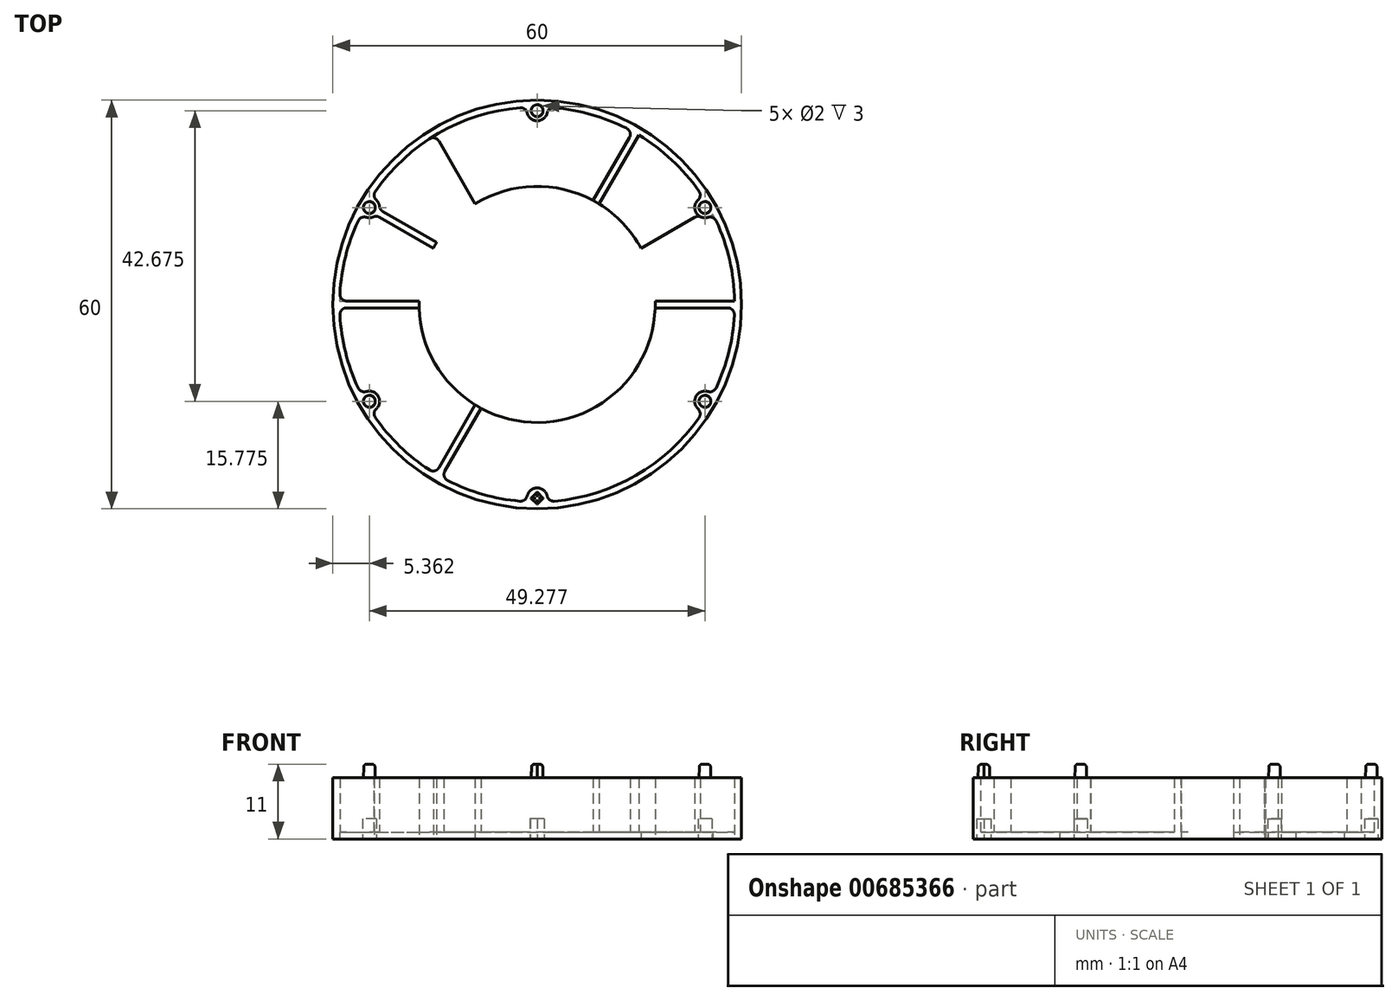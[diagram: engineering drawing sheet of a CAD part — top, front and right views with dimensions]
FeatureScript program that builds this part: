
annotation { "Feature Type Name" : "Feature", "Feature Type Description" : "" }
export const myFeature = defineFeature(function(context is Context, id is Id, definition is map)
    precondition{}
    {
        {
            var Q0;
            Q0=qCreatedBy(makeId("Top.planeOp"),FACE);
            var sketch = newSketch(context, id + "F0", { "sketchPlane" : qUnion([Q0])});
            skCircle(sketch, "E0", {"center": v(0, 0) * mm, "radius": 30 * mm});
            skCircle(sketch, "E1.0", {"center": v(0, 0) * mm, "radius": 29 * mm});
            skLineSegment(sketch, "E2.bottom", {"start": v(14.56, 26.23) * mm, "end": v(15.43, 25.73) * mm});
            skLineSegment(sketch, "E2.top", {"start": v(-15.43, -25.73) * mm, "end": v(-14.56, -26.23) * mm});
            skLineSegment(sketch, "E2.left", {"start": v(14.56, 26.23) * mm, "end": v(-15.43, -25.73) * mm});
            skLineSegment(sketch, "E2.right", {"start": v(15.43, 25.73) * mm, "end": v(-14.56, -26.23) * mm});
            skLineSegment(sketch, "E3.bottom", {"start": v(25.73, 15.43) * mm, "end": v(26.23, 14.56) * mm});
            skLineSegment(sketch, "E3.top", {"start": v(-26.23, -14.56) * mm, "end": v(-25.73, -15.43) * mm});
            skLineSegment(sketch, "E3.left", {"start": v(25.73, 15.43) * mm, "end": v(-26.23, -14.56) * mm});
            skLineSegment(sketch, "E3.right", {"start": v(26.23, 14.56) * mm, "end": v(-25.73, -15.43) * mm});
            skLineSegment(sketch, "E4", {"start": v(-38.35, 0) * mm, "end": v(39.17, 0) * mm, "construction": true});
            skLineSegment(sketch, "E5", {"start": v(0, 42.5) * mm, "end": v(0, -42.47) * mm, "construction": true});
            skLineSegment(sketch, "E6.bottom", {"start": v(-30, 0.5) * mm, "end": v(30, 0.5) * mm});
            skLineSegment(sketch, "E6.top", {"start": v(-30, -0.5) * mm, "end": v(30, -0.5) * mm});
            skLineSegment(sketch, "E6.left", {"start": v(-30, 0.5) * mm, "end": v(-30, -0.5) * mm});
            skLineSegment(sketch, "E6.right", {"start": v(30, 0.5) * mm, "end": v(30, -0.5) * mm});
            skLineSegment(sketch, "E7.bottom", {"start": v(-25.73, 15.43) * mm, "end": v(26.23, -14.56) * mm});
            skLineSegment(sketch, "E7.top", {"start": v(-26.23, 14.56) * mm, "end": v(25.73, -15.43) * mm});
            skLineSegment(sketch, "E7.left", {"start": v(-25.73, 15.43) * mm, "end": v(-26.23, 14.56) * mm});
            skLineSegment(sketch, "E7.right", {"start": v(26.23, -14.56) * mm, "end": v(25.73, -15.43) * mm});
            skLineSegment(sketch, "E8.bottom", {"start": v(-0.5, 30) * mm, "end": v(0.5, 30) * mm});
            skLineSegment(sketch, "E8.top", {"start": v(-0.5, -30) * mm, "end": v(0.5, -30) * mm});
            skLineSegment(sketch, "E8.left", {"start": v(-0.5, 30) * mm, "end": v(-0.5, -30) * mm});
            skLineSegment(sketch, "E8.right", {"start": v(0.5, 30) * mm, "end": v(0.5, -30) * mm});
            skLineSegment(sketch, "E9.bottom", {"start": v(-15.43, 25.73) * mm, "end": v(-14.56, 26.23) * mm});
            skLineSegment(sketch, "E9.top", {"start": v(14.56, -26.23) * mm, "end": v(15.43, -25.73) * mm});
            skLineSegment(sketch, "E9.left", {"start": v(-15.43, 25.73) * mm, "end": v(14.56, -26.23) * mm});
            skLineSegment(sketch, "E9.right", {"start": v(-14.56, 26.23) * mm, "end": v(15.43, -25.73) * mm});
            skCircle(sketch, "E10", {"center": v(0, 0) * mm, "radius": 17.33 * mm});
            skSolve(sketch);
        }
        {
            var Q0;
            Q0=qCreatedBy(makeId("Top.planeOp"),FACE);
            var sketch = newSketch(context, id + "F1", { "sketchPlane" : qUnion([Q0])});
            skCircle(sketch, "E11", {"center": v(0, 0) * mm, "radius": 30 * mm});
            skCircle(sketch, "E12", {"center": v(0, 0) * mm, "radius": 29 * mm});
            skSolve(sketch);
        }
        {
            var Q0;
            Q0=makeQuery(id+"F1.imprint","IMPRINT",FACE,{"disambiguationData":[TD([[makeQuery(id+"F1.imprint","IMPRINT",EDGE,{"derivedFrom":sQuery(id+"F1.wireOp",EDGE,"E11")}),1.0]])]});
            extrude(context, id + "F2", {"entities" : qUnion([Q0]), "depth" : 9 * mm, "offsetDistance" : 25 * mm});
        }
        {
            var Q0;
            {var subQ0=sQuery(id+"F0.wireOp",EDGE,"E7.bottom");var subQ1=sQuery(id+"F0.wireOp",EDGE,"E1.0");var subQ2=makeQuery(id+"F0.imprint","INTERSECT",VERTEX,{"disambiguationData":[OD(0.0)],"derivedFrom":[subQ1,subQ0]});Q0=makeQuery(id+"F0.imprint","IMPRINT",FACE,{"disambiguationData":[TD([[makeQuery(id+"F0.imprint","IMPRINT",EDGE,{"disambiguationData":[TD([[subQ2,-1.0]])],"derivedFrom":subQ1}),1.0]])]});}
            var Q1;
            {var subQ0=sQuery(id+"F0.wireOp",EDGE,"E2.right");var subQ1=sQuery(id+"F0.wireOp",EDGE,"E1.0");var subQ2=makeQuery(id+"F0.imprint","INTERSECT",VERTEX,{"disambiguationData":[OD(0.0)],"derivedFrom":[subQ1,subQ0]});Q1=makeQuery(id+"F0.imprint","IMPRINT",FACE,{"disambiguationData":[TD([[makeQuery(id+"F0.imprint","IMPRINT",EDGE,{"disambiguationData":[TD([[subQ2,-1.0]])],"derivedFrom":subQ1}),1.0]])]});}
            var Q2;
            {var subQ0=sQuery(id+"F0.wireOp",EDGE,"E6.bottom");var subQ1=sQuery(id+"F0.wireOp",EDGE,"E1.0");var subQ2=makeQuery(id+"F0.imprint","INTERSECT",VERTEX,{"disambiguationData":[OD(0.0)],"derivedFrom":[subQ1,subQ0]});Q2=makeQuery(id+"F0.imprint","IMPRINT",FACE,{"disambiguationData":[TD([[makeQuery(id+"F0.imprint","IMPRINT",EDGE,{"disambiguationData":[TD([[subQ2,1.0]])],"derivedFrom":subQ1}),1.0]])]});}
            var Q3;
            {var subQ0=sQuery(id+"F0.wireOp",EDGE,"E2.left");var subQ1=sQuery(id+"F0.wireOp",EDGE,"E1.0");var subQ2=makeQuery(id+"F0.imprint","INTERSECT",VERTEX,{"disambiguationData":[OD(1.0)],"derivedFrom":[subQ1,subQ0]});Q3=makeQuery(id+"F0.imprint","IMPRINT",FACE,{"disambiguationData":[TD([[makeQuery(id+"F0.imprint","IMPRINT",EDGE,{"disambiguationData":[TD([[subQ2,-1.0]])],"derivedFrom":subQ1}),1.0]])]});}
            var Q4;
            {var subQ0=sQuery(id+"F0.wireOp",EDGE,"E6.bottom");var subQ1=sQuery(id+"F0.wireOp",EDGE,"E1.0");var subQ2=makeQuery(id+"F0.imprint","INTERSECT",VERTEX,{"disambiguationData":[OD(1.0)],"derivedFrom":[subQ1,subQ0]});Q4=makeQuery(id+"F0.imprint","IMPRINT",FACE,{"disambiguationData":[TD([[makeQuery(id+"F0.imprint","IMPRINT",EDGE,{"disambiguationData":[TD([[subQ2,-1.0]])],"derivedFrom":subQ1}),1.0]])]});}
            extrude(context, id + "F3", {"entities" : qUnion([Q0, Q1, Q2, Q3, Q4]), "operationType" : NewBodyOperationType.ADD, "depth" : 9 * mm, "offsetDistance" : 25 * mm});
        }
        {
            var Q0;
            Q0=makeQuery(id+"F1.imprint","IMPRINT",FACE,{"disambiguationData":[TD([[makeQuery(id+"F1.imprint","IMPRINT",EDGE,{"derivedFrom":sQuery(id+"F1.wireOp",EDGE,"E11")}),1.0]])]});
            var Q1;
            Q1=makeQuery(id+"F1.imprint","IMPRINT",FACE,{"disambiguationData":[TD([[makeQuery(id+"F1.imprint","IMPRINT",EDGE,{"derivedFrom":sQuery(id+"F1.wireOp",EDGE,"E12")}),1.0]])]});
            extrude(context, id + "F4", {"entities" : qUnion([Q0, Q1]), "operationType" : NewBodyOperationType.ADD, "depth" : 1 * mm, "offsetDistance" : 25 * mm});
        }
        {
            var Q0;
            {var subQ0=sQuery(id+"F0.wireOp",EDGE,"E3.right");var subQ1=sQuery(id+"F0.wireOp",EDGE,"E1.0");var subQ2=makeQuery(id+"F0.imprint","INTERSECT",VERTEX,{"disambiguationData":[OD(0.0)],"derivedFrom":[subQ1,subQ0]});Q0=makeQuery(id+"F0.imprint","IMPRINT",FACE,{"disambiguationData":[TD([[makeQuery(id+"F0.imprint","IMPRINT",EDGE,{"disambiguationData":[TD([[subQ2,1.0]])],"derivedFrom":subQ1}),1.0]])]});}
            var Q1;
            {var subQ0=sQuery(id+"F0.wireOp",EDGE,"E9.left");var subQ1=sQuery(id+"F0.wireOp",EDGE,"E1.0");var subQ2=makeQuery(id+"F0.imprint","INTERSECT",VERTEX,{"disambiguationData":[OD(0.0)],"derivedFrom":[subQ1,subQ0]});Q1=makeQuery(id+"F0.imprint","IMPRINT",FACE,{"disambiguationData":[TD([[makeQuery(id+"F0.imprint","IMPRINT",EDGE,{"disambiguationData":[TD([[subQ2,-1.0]])],"derivedFrom":subQ1}),1.0]])]});}
            var Q2;
            {var subQ0=sQuery(id+"F0.wireOp",EDGE,"E7.top");var subQ1=sQuery(id+"F0.wireOp",EDGE,"E1.0");var subQ2=makeQuery(id+"F0.imprint","INTERSECT",VERTEX,{"disambiguationData":[OD(0.0)],"derivedFrom":[subQ1,subQ0]});Q2=makeQuery(id+"F0.imprint","IMPRINT",FACE,{"disambiguationData":[TD([[makeQuery(id+"F0.imprint","IMPRINT",EDGE,{"disambiguationData":[TD([[subQ2,-1.0]])],"derivedFrom":subQ1}),1.0]])]});}
            extrude(context, id + "F5", {"entities" : qUnion([Q0, Q1, Q2]), "operationType" : NewBodyOperationType.REMOVE, "depth" : 1 * mm, "offsetDistance" : 25 * mm});
        }
        {
            var Q0;
            Q0=qCreatedBy(makeId("Top.planeOp"),FACE);
            var sketch = newSketch(context, id + "F6", { "sketchPlane" : qUnion([Q0])});
            skCircle(sketch, "E13", {"center": v(0, 0) * mm, "radius": 28.45 * mm});
            skLineSegment(sketch, "E14", {"start": v(0, 28.45) * mm, "end": v(0, -28.45) * mm, "construction": true});
            skLineSegment(sketch, "E15", {"start": v(24.64, 14.22) * mm, "end": v(0, 0) * mm, "construction": true});
            skLineSegment(sketch, "E16", {"start": v(14.23, 24.64) * mm, "end": v(0, 0) * mm, "construction": true});
            skLineSegment(sketch, "E17", {"start": v(0, 0) * mm, "end": v(28.45, 0) * mm, "construction": true});
            skLineSegment(sketch, "E18", {"start": v(0, 0) * mm, "end": v(24.64, -14.22) * mm, "construction": true});
            skLineSegment(sketch, "E19", {"start": v(0, 0) * mm, "end": v(14.23, -24.64) * mm, "construction": true});
            skLineSegment(sketch, "E20", {"start": v(0, 0) * mm, "end": v(-14.23, 24.64) * mm, "construction": true});
            skLineSegment(sketch, "E21", {"start": v(0, 0) * mm, "end": v(-24.64, 14.22) * mm, "construction": true});
            skLineSegment(sketch, "E22", {"start": v(0, 0) * mm, "end": v(-28.45, 0) * mm, "construction": true});
            skLineSegment(sketch, "E23", {"start": v(0, 0) * mm, "end": v(-24.64, -14.23) * mm, "construction": true});
            skLineSegment(sketch, "E24", {"start": v(0, 0) * mm, "end": v(-14.22, -24.64) * mm, "construction": true});
            skCircle(sketch, "E25", {"center": v(0, 28.45) * mm, "radius": 1.5 * mm});
            skCircle(sketch, "E26", {"center": v(24.64, 14.22) * mm, "radius": 1.5 * mm});
            skCircle(sketch, "E27", {"center": v(24.64, -14.22) * mm, "radius": 1.5 * mm});
            skCircle(sketch, "E28", {"center": v(0, -28.45) * mm, "radius": 1.5 * mm});
            skCircle(sketch, "E29", {"center": v(-24.64, -14.23) * mm, "radius": 1.5 * mm});
            skCircle(sketch, "E30", {"center": v(-24.64, 14.22) * mm, "radius": 1.5 * mm});
            skCircle(sketch, "E31", {"center": v(-24.64, 14.22) * mm, "radius": 1 * mm});
            skCircle(sketch, "E32", {"center": v(0, 28.45) * mm, "radius": 1 * mm});
            skCircle(sketch, "E33", {"center": v(24.64, 14.22) * mm, "radius": 1 * mm});
            skCircle(sketch, "E34", {"center": v(24.64, -14.22) * mm, "radius": 1 * mm});
            skCircle(sketch, "E35", {"center": v(-24.64, -14.23) * mm, "radius": 1 * mm});
            skLineSegment(sketch, "E36.bottom", {"start": v(1.06, -28.45) * mm, "end": v(0, -29.51) * mm});
            skLineSegment(sketch, "E36.top", {"start": v(0, -27.39) * mm, "end": v(-1.06, -28.45) * mm});
            skLineSegment(sketch, "E36.left", {"start": v(1.06, -28.45) * mm, "end": v(0, -27.39) * mm});
            skLineSegment(sketch, "E36.right", {"start": v(0, -29.51) * mm, "end": v(-1.06, -28.45) * mm});
            skSolve(sketch);
        }
        {
            var Q0;
            {var subQ0=sQuery(id+"F6.wireOp",EDGE,"E30");var subQ1=sQuery(id+"F6.wireOp",EDGE,"E13");var subQ2=makeQuery(id+"F6.imprint","INTERSECT",VERTEX,{"disambiguationData":[OD(0.0)],"derivedFrom":[subQ1,subQ0]});Q0=makeQuery(id+"F6.imprint","IMPRINT",FACE,{"disambiguationData":[TD([[makeQuery(id+"F6.imprint","IMPRINT",EDGE,{"disambiguationData":[TD([[subQ2,-1.0]])],"derivedFrom":subQ1}),1.0]])]});}
            var Q1;
            {var subQ0=sQuery(id+"F6.wireOp",EDGE,"E30");var subQ1=sQuery(id+"F6.wireOp",EDGE,"E13");var subQ2=makeQuery(id+"F6.imprint","INTERSECT",VERTEX,{"disambiguationData":[OD(0.0)],"derivedFrom":[subQ1,subQ0]});Q1=makeQuery(id+"F6.imprint","IMPRINT",FACE,{"disambiguationData":[TD([[makeQuery(id+"F6.imprint","IMPRINT",EDGE,{"disambiguationData":[TD([[subQ2,-1.0]])],"derivedFrom":subQ1}),-1.0]])]});}
            var Q2;
            {var subQ0=sQuery(id+"F6.wireOp",EDGE,"E25");var subQ1=sQuery(id+"F6.wireOp",EDGE,"E13");var subQ2=makeQuery(id+"F6.imprint","INTERSECT",VERTEX,{"disambiguationData":[OD(0.0)],"derivedFrom":[subQ1,subQ0]});Q2=makeQuery(id+"F6.imprint","IMPRINT",FACE,{"disambiguationData":[TD([[makeQuery(id+"F6.imprint","IMPRINT",EDGE,{"disambiguationData":[TD([[subQ2,-1.0]])],"derivedFrom":subQ1}),1.0]])]});}
            var Q3;
            {var subQ0=sQuery(id+"F6.wireOp",EDGE,"E25");var subQ1=sQuery(id+"F6.wireOp",EDGE,"E13");var subQ2=makeQuery(id+"F6.imprint","INTERSECT",VERTEX,{"disambiguationData":[OD(0.0)],"derivedFrom":[subQ1,subQ0]});Q3=makeQuery(id+"F6.imprint","IMPRINT",FACE,{"disambiguationData":[TD([[makeQuery(id+"F6.imprint","IMPRINT",EDGE,{"disambiguationData":[TD([[subQ2,-1.0]])],"derivedFrom":subQ1}),-1.0]])]});}
            var Q4;
            {var subQ0=sQuery(id+"F6.wireOp",EDGE,"E26");var subQ1=sQuery(id+"F6.wireOp",EDGE,"E13");var subQ2=makeQuery(id+"F6.imprint","INTERSECT",VERTEX,{"disambiguationData":[OD(0.0)],"derivedFrom":[subQ1,subQ0]});Q4=makeQuery(id+"F6.imprint","IMPRINT",FACE,{"disambiguationData":[TD([[makeQuery(id+"F6.imprint","IMPRINT",EDGE,{"disambiguationData":[TD([[subQ2,-1.0]])],"derivedFrom":subQ1}),-1.0]])]});}
            var Q5;
            {var subQ0=sQuery(id+"F6.wireOp",EDGE,"E26");var subQ1=sQuery(id+"F6.wireOp",EDGE,"E13");var subQ2=makeQuery(id+"F6.imprint","INTERSECT",VERTEX,{"disambiguationData":[OD(0.0)],"derivedFrom":[subQ1,subQ0]});Q5=makeQuery(id+"F6.imprint","IMPRINT",FACE,{"disambiguationData":[TD([[makeQuery(id+"F6.imprint","IMPRINT",EDGE,{"disambiguationData":[TD([[subQ2,-1.0]])],"derivedFrom":subQ1}),1.0]])]});}
            var Q6;
            {var subQ0=sQuery(id+"F6.wireOp",EDGE,"E29");var subQ1=sQuery(id+"F6.wireOp",EDGE,"E13");var subQ2=makeQuery(id+"F6.imprint","INTERSECT",VERTEX,{"disambiguationData":[OD(0.0)],"derivedFrom":[subQ1,subQ0]});Q6=makeQuery(id+"F6.imprint","IMPRINT",FACE,{"disambiguationData":[TD([[makeQuery(id+"F6.imprint","IMPRINT",EDGE,{"disambiguationData":[TD([[subQ2,-1.0]])],"derivedFrom":subQ1}),1.0]])]});}
            var Q7;
            {var subQ0=sQuery(id+"F6.wireOp",EDGE,"E29");var subQ1=sQuery(id+"F6.wireOp",EDGE,"E13");var subQ2=makeQuery(id+"F6.imprint","INTERSECT",VERTEX,{"disambiguationData":[OD(0.0)],"derivedFrom":[subQ1,subQ0]});Q7=makeQuery(id+"F6.imprint","IMPRINT",FACE,{"disambiguationData":[TD([[makeQuery(id+"F6.imprint","IMPRINT",EDGE,{"disambiguationData":[TD([[subQ2,-1.0]])],"derivedFrom":subQ1}),-1.0]])]});}
            var Q8;
            {var subQ3=sQuery(id+"F6.wireOp",EDGE,"E13");var subQ5=sQuery(id+"F6.wireOp",EDGE,"E28");var subQ6=makeQuery(id+"F6.imprint","INTERSECT",VERTEX,{"disambiguationData":[OD(0.0)],"derivedFrom":[subQ3,subQ5]});Q8=makeQuery(id+"F6.imprint","IMPRINT",FACE,{"disambiguationData":[TD([[makeQuery(id+"F6.imprint","IMPRINT",EDGE,{"disambiguationData":[TD([[subQ6,-1.0]])],"derivedFrom":subQ3}),1.0]])]});}
            var Q9;
            {var subQ6=sQuery(id+"F6.wireOp",EDGE,"E36.bottom");Q9=makeQuery(id+"F6.imprint","IMPRINT",FACE,{"disambiguationData":[TD([[makeQuery(id+"F6.imprint","IMPRINT",EDGE,{"derivedFrom":subQ6}),1.0]])]});}
            var Q10;
            {var subQ0=sQuery(id+"F6.wireOp",EDGE,"E27");var subQ1=sQuery(id+"F6.wireOp",EDGE,"E13");var subQ2=makeQuery(id+"F6.imprint","INTERSECT",VERTEX,{"disambiguationData":[OD(0.0)],"derivedFrom":[subQ1,subQ0]});Q10=makeQuery(id+"F6.imprint","IMPRINT",FACE,{"disambiguationData":[TD([[makeQuery(id+"F6.imprint","IMPRINT",EDGE,{"disambiguationData":[TD([[subQ2,-1.0]])],"derivedFrom":subQ1}),-1.0]])]});}
            var Q11;
            {var subQ0=sQuery(id+"F6.wireOp",EDGE,"E27");var subQ1=sQuery(id+"F6.wireOp",EDGE,"E13");var subQ2=makeQuery(id+"F6.imprint","INTERSECT",VERTEX,{"disambiguationData":[OD(0.0)],"derivedFrom":[subQ1,subQ0]});Q11=makeQuery(id+"F6.imprint","IMPRINT",FACE,{"disambiguationData":[TD([[makeQuery(id+"F6.imprint","IMPRINT",EDGE,{"disambiguationData":[TD([[subQ2,-1.0]])],"derivedFrom":subQ1}),1.0]])]});}
            var Q12;
            {var subQ0=sQuery(id+"F6.wireOp",EDGE,"E31");var subQ1=sQuery(id+"F6.wireOp",EDGE,"E13");var subQ2=makeQuery(id+"F6.imprint","INTERSECT",VERTEX,{"disambiguationData":[OD(0.0)],"derivedFrom":[subQ1,subQ0]});Q12=makeQuery(id+"F6.imprint","IMPRINT",FACE,{"disambiguationData":[TD([[makeQuery(id+"F6.imprint","IMPRINT",EDGE,{"disambiguationData":[TD([[subQ2,-1.0]])],"derivedFrom":subQ1}),1.0]])]});}
            var Q13;
            {var subQ0=sQuery(id+"F6.wireOp",EDGE,"E31");var subQ1=sQuery(id+"F6.wireOp",EDGE,"E13");var subQ2=makeQuery(id+"F6.imprint","INTERSECT",VERTEX,{"disambiguationData":[OD(0.0)],"derivedFrom":[subQ1,subQ0]});Q13=makeQuery(id+"F6.imprint","IMPRINT",FACE,{"disambiguationData":[TD([[makeQuery(id+"F6.imprint","IMPRINT",EDGE,{"disambiguationData":[TD([[subQ2,-1.0]])],"derivedFrom":subQ1}),-1.0]])]});}
            var Q14;
            {var subQ0=sQuery(id+"F6.wireOp",EDGE,"E32");var subQ1=sQuery(id+"F6.wireOp",EDGE,"E13");var subQ2=makeQuery(id+"F6.imprint","INTERSECT",VERTEX,{"disambiguationData":[OD(0.0)],"derivedFrom":[subQ1,subQ0]});Q14=makeQuery(id+"F6.imprint","IMPRINT",FACE,{"disambiguationData":[TD([[makeQuery(id+"F6.imprint","IMPRINT",EDGE,{"disambiguationData":[TD([[subQ2,-1.0]])],"derivedFrom":subQ1}),-1.0]])]});}
            var Q15;
            {var subQ0=sQuery(id+"F6.wireOp",EDGE,"E32");var subQ1=sQuery(id+"F6.wireOp",EDGE,"E13");var subQ2=makeQuery(id+"F6.imprint","INTERSECT",VERTEX,{"disambiguationData":[OD(0.0)],"derivedFrom":[subQ1,subQ0]});Q15=makeQuery(id+"F6.imprint","IMPRINT",FACE,{"disambiguationData":[TD([[makeQuery(id+"F6.imprint","IMPRINT",EDGE,{"disambiguationData":[TD([[subQ2,-1.0]])],"derivedFrom":subQ1}),1.0]])]});}
            var Q16;
            {var subQ0=sQuery(id+"F6.wireOp",EDGE,"E33");var subQ1=sQuery(id+"F6.wireOp",EDGE,"E13");var subQ2=makeQuery(id+"F6.imprint","INTERSECT",VERTEX,{"disambiguationData":[OD(0.0)],"derivedFrom":[subQ1,subQ0]});Q16=makeQuery(id+"F6.imprint","IMPRINT",FACE,{"disambiguationData":[TD([[makeQuery(id+"F6.imprint","IMPRINT",EDGE,{"disambiguationData":[TD([[subQ2,-1.0]])],"derivedFrom":subQ1}),-1.0]])]});}
            var Q17;
            {var subQ0=sQuery(id+"F6.wireOp",EDGE,"E33");var subQ1=sQuery(id+"F6.wireOp",EDGE,"E13");var subQ2=makeQuery(id+"F6.imprint","INTERSECT",VERTEX,{"disambiguationData":[OD(0.0)],"derivedFrom":[subQ1,subQ0]});Q17=makeQuery(id+"F6.imprint","IMPRINT",FACE,{"disambiguationData":[TD([[makeQuery(id+"F6.imprint","IMPRINT",EDGE,{"disambiguationData":[TD([[subQ2,-1.0]])],"derivedFrom":subQ1}),1.0]])]});}
            var Q18;
            {var subQ0=sQuery(id+"F6.wireOp",EDGE,"E34");var subQ1=sQuery(id+"F6.wireOp",EDGE,"E13");var subQ2=makeQuery(id+"F6.imprint","INTERSECT",VERTEX,{"disambiguationData":[OD(0.0)],"derivedFrom":[subQ1,subQ0]});Q18=makeQuery(id+"F6.imprint","IMPRINT",FACE,{"disambiguationData":[TD([[makeQuery(id+"F6.imprint","IMPRINT",EDGE,{"disambiguationData":[TD([[subQ2,-1.0]])],"derivedFrom":subQ1}),-1.0]])]});}
            var Q19;
            {var subQ0=sQuery(id+"F6.wireOp",EDGE,"E34");var subQ1=sQuery(id+"F6.wireOp",EDGE,"E13");var subQ2=makeQuery(id+"F6.imprint","INTERSECT",VERTEX,{"disambiguationData":[OD(0.0)],"derivedFrom":[subQ1,subQ0]});Q19=makeQuery(id+"F6.imprint","IMPRINT",FACE,{"disambiguationData":[TD([[makeQuery(id+"F6.imprint","IMPRINT",EDGE,{"disambiguationData":[TD([[subQ2,-1.0]])],"derivedFrom":subQ1}),1.0]])]});}
            var Q20;
            {var subQ1=sQuery(id+"F6.wireOp",EDGE,"E36.bottom");Q20=makeQuery(id+"F6.imprint","IMPRINT",FACE,{"disambiguationData":[TD([[makeQuery(id+"F6.imprint","IMPRINT",EDGE,{"derivedFrom":subQ1}),-1.0]])]});}
            var Q21;
            {var subQ0=sQuery(id+"F6.wireOp",EDGE,"E35");var subQ1=sQuery(id+"F6.wireOp",EDGE,"E13");var subQ2=makeQuery(id+"F6.imprint","INTERSECT",VERTEX,{"disambiguationData":[OD(0.0)],"derivedFrom":[subQ1,subQ0]});Q21=makeQuery(id+"F6.imprint","IMPRINT",FACE,{"disambiguationData":[TD([[makeQuery(id+"F6.imprint","IMPRINT",EDGE,{"disambiguationData":[TD([[subQ2,-1.0]])],"derivedFrom":subQ1}),-1.0]])]});}
            var Q22;
            {var subQ0=sQuery(id+"F6.wireOp",EDGE,"E35");var subQ1=sQuery(id+"F6.wireOp",EDGE,"E13");var subQ2=makeQuery(id+"F6.imprint","INTERSECT",VERTEX,{"disambiguationData":[OD(0.0)],"derivedFrom":[subQ1,subQ0]});Q22=makeQuery(id+"F6.imprint","IMPRINT",FACE,{"disambiguationData":[TD([[makeQuery(id+"F6.imprint","IMPRINT",EDGE,{"disambiguationData":[TD([[subQ2,-1.0]])],"derivedFrom":subQ1}),1.0]])]});}
            var Q23;
            {var subQ0=sQuery(id+"F6.wireOp",EDGE,"E36.top");var subQ1=sQuery(id+"F6.wireOp",EDGE,"E13");var subQ2=makeQuery(id+"F6.imprint","INTERSECT",VERTEX,{"derivedFrom":[subQ1,subQ0]});Q23=makeQuery(id+"F6.imprint","IMPRINT",FACE,{"disambiguationData":[TD([[makeQuery(id+"F6.imprint","IMPRINT",EDGE,{"disambiguationData":[TD([[subQ2,-1.0]])],"derivedFrom":subQ1}),1.0]])]});}
            extrude(context, id + "F7", {"entities" : qUnion([Q0, Q1, Q2, Q3, Q4, Q5, Q6, Q7, Q8, Q9, Q10, Q11, Q12, Q13, Q14, Q15, Q16, Q17, Q18, Q19, Q20, Q21, Q22, Q23]), "operationType" : NewBodyOperationType.ADD, "depth" : 9 * mm, "offsetDistance" : 25 * mm});
        }
        {
            var Q0;
            {var subQ0=sQuery(id+"F0.wireOp",EDGE,"E8.right");var subQ1=sQuery(id+"F0.wireOp",EDGE,"E1.0");Q0=makeQuery(id+"F3.opExtrude","SWEPT_EDGE",EDGE,{"disambiguationData":[OSD([subQ1,subQ0]),TDD([makeQuery(id+"F0.imprint","INTERSECT",VERTEX,{"disambiguationData":[OD(1.0)],"derivedFrom":[subQ1,subQ0]})])]});}
            var Q1;
            {var subQ0=sQuery(id+"F0.wireOp",EDGE,"E2.left");var subQ1=sQuery(id+"F0.wireOp",EDGE,"E1.0");Q1=makeQuery(id+"F3.opExtrude","SWEPT_EDGE",EDGE,{"disambiguationData":[OSD([subQ1,subQ0]),TDD([makeQuery(id+"F0.imprint","INTERSECT",VERTEX,{"disambiguationData":[OD(1.0)],"derivedFrom":[subQ1,subQ0]})])]});}
            var Q2;
            {var subQ0=sQuery(id+"F0.wireOp",EDGE,"E3.left");var subQ1=sQuery(id+"F0.wireOp",EDGE,"E1.0");Q2=makeQuery(id+"F3.opExtrude","SWEPT_EDGE",EDGE,{"disambiguationData":[OSD([subQ1,subQ0]),TDD([makeQuery(id+"F0.imprint","INTERSECT",VERTEX,{"disambiguationData":[OD(1.0)],"derivedFrom":[subQ1,subQ0]})])]});}
            var Q3;
            {var subQ0=sQuery(id+"F0.wireOp",EDGE,"E6.bottom");var subQ1=sQuery(id+"F0.wireOp",EDGE,"E1.0");Q3=makeQuery(id+"F3.opExtrude","SWEPT_EDGE",EDGE,{"disambiguationData":[OSD([subQ1,subQ0]),TDD([makeQuery(id+"F0.imprint","INTERSECT",VERTEX,{"disambiguationData":[OD(1.0)],"derivedFrom":[subQ1,subQ0]})])]});}
            var Q4;
            {var subQ0=sQuery(id+"F0.wireOp",EDGE,"E9.right");var subQ1=sQuery(id+"F0.wireOp",EDGE,"E1.0");Q4=makeQuery(id+"F3.opExtrude","SWEPT_EDGE",EDGE,{"disambiguationData":[OSD([subQ1,subQ0]),TDD([makeQuery(id+"F0.imprint","INTERSECT",VERTEX,{"disambiguationData":[OD(1.0)],"derivedFrom":[subQ1,subQ0]})])]});}
            var Q5;
            {var subQ0=sQuery(id+"F0.wireOp",EDGE,"E7.bottom");var subQ1=sQuery(id+"F0.wireOp",EDGE,"E1.0");Q5=makeQuery(id+"F3.opExtrude","SWEPT_EDGE",EDGE,{"disambiguationData":[OSD([subQ1,subQ0]),TDD([makeQuery(id+"F0.imprint","INTERSECT",VERTEX,{"disambiguationData":[OD(1.0)],"derivedFrom":[subQ1,subQ0]})])]});}
            var Q6;
            {var subQ0=sQuery(id+"F0.wireOp",EDGE,"E8.left");var subQ1=sQuery(id+"F0.wireOp",EDGE,"E1.0");Q6=makeQuery(id+"F3.opExtrude","SWEPT_EDGE",EDGE,{"disambiguationData":[OSD([subQ1,subQ0]),TDD([makeQuery(id+"F0.imprint","INTERSECT",VERTEX,{"disambiguationData":[OD(0.0)],"derivedFrom":[subQ1,subQ0]})])]});}
            var Q7;
            {var subQ0=sQuery(id+"F0.wireOp",EDGE,"E2.left");var subQ1=sQuery(id+"F0.wireOp",EDGE,"E1.0");Q7=makeQuery(id+"F3.opExtrude","SWEPT_EDGE",EDGE,{"disambiguationData":[OSD([subQ1,subQ0]),TDD([makeQuery(id+"F0.imprint","INTERSECT",VERTEX,{"disambiguationData":[OD(0.0)],"derivedFrom":[subQ1,subQ0]})])]});}
            var Q8;
            {var subQ0=sQuery(id+"F0.wireOp",EDGE,"E3.left");var subQ1=sQuery(id+"F0.wireOp",EDGE,"E1.0");Q8=makeQuery(id+"F3.opExtrude","SWEPT_EDGE",EDGE,{"disambiguationData":[OSD([subQ1,subQ0]),TDD([makeQuery(id+"F0.imprint","INTERSECT",VERTEX,{"disambiguationData":[OD(0.0)],"derivedFrom":[subQ1,subQ0]})])]});}
            var Q9;
            {var subQ0=sQuery(id+"F0.wireOp",EDGE,"E6.top");var subQ1=sQuery(id+"F0.wireOp",EDGE,"E1.0");Q9=makeQuery(id+"F3.opExtrude","SWEPT_EDGE",EDGE,{"disambiguationData":[OSD([subQ1,subQ0]),TDD([makeQuery(id+"F0.imprint","INTERSECT",VERTEX,{"disambiguationData":[OD(1.0)],"derivedFrom":[subQ1,subQ0]})])]});}
            var Q10;
            {var subQ0=sQuery(id+"F0.wireOp",EDGE,"E7.top");var subQ1=sQuery(id+"F0.wireOp",EDGE,"E1.0");Q10=makeQuery(id+"F3.opExtrude","SWEPT_EDGE",EDGE,{"disambiguationData":[OSD([subQ1,subQ0]),TDD([makeQuery(id+"F0.imprint","INTERSECT",VERTEX,{"disambiguationData":[OD(0.0)],"derivedFrom":[subQ1,subQ0]})])]});}
            var Q11;
            {var subQ0=sQuery(id+"F0.wireOp",EDGE,"E6.top");var subQ1=sQuery(id+"F0.wireOp",EDGE,"E1.0");Q11=makeQuery(id+"F3.opExtrude","SWEPT_EDGE",EDGE,{"disambiguationData":[OSD([subQ1,subQ0]),TDD([makeQuery(id+"F0.imprint","INTERSECT",VERTEX,{"disambiguationData":[OD(0.0)],"derivedFrom":[subQ1,subQ0]})])]});}
            var Q12;
            {var subQ0=sQuery(id+"F0.wireOp",EDGE,"E9.left");var subQ1=sQuery(id+"F0.wireOp",EDGE,"E1.0");Q12=makeQuery(id+"F3.opExtrude","SWEPT_EDGE",EDGE,{"disambiguationData":[OSD([subQ1,subQ0]),TDD([makeQuery(id+"F0.imprint","INTERSECT",VERTEX,{"disambiguationData":[OD(0.0)],"derivedFrom":[subQ1,subQ0]})])]});}
            var Q13;
            {var subQ0=sQuery(id+"F0.wireOp",EDGE,"E8.right");var subQ1=sQuery(id+"F0.wireOp",EDGE,"E1.0");Q13=makeQuery(id+"F3.opExtrude","SWEPT_EDGE",EDGE,{"disambiguationData":[OSD([subQ1,subQ0]),TDD([makeQuery(id+"F0.imprint","INTERSECT",VERTEX,{"disambiguationData":[OD(0.0)],"derivedFrom":[subQ1,subQ0]})])]});}
            var Q14;
            {var subQ0=sQuery(id+"F0.wireOp",EDGE,"E7.bottom");var subQ1=sQuery(id+"F0.wireOp",EDGE,"E1.0");Q14=makeQuery(id+"F3.opExtrude","SWEPT_EDGE",EDGE,{"disambiguationData":[OSD([subQ1,subQ0]),TDD([makeQuery(id+"F0.imprint","INTERSECT",VERTEX,{"disambiguationData":[OD(0.0)],"derivedFrom":[subQ1,subQ0]})])]});}
            var Q15;
            {var subQ0=sQuery(id+"F0.wireOp",EDGE,"E9.right");var subQ1=sQuery(id+"F0.wireOp",EDGE,"E1.0");Q15=makeQuery(id+"F3.opExtrude","SWEPT_EDGE",EDGE,{"disambiguationData":[OSD([subQ1,subQ0]),TDD([makeQuery(id+"F0.imprint","INTERSECT",VERTEX,{"disambiguationData":[OD(0.0)],"derivedFrom":[subQ1,subQ0]})])]});}
            var Q16;
            {var subQ0=sQuery(id+"F0.wireOp",EDGE,"E3.right");var subQ1=sQuery(id+"F0.wireOp",EDGE,"E1.0");Q16=makeQuery(id+"F3.opExtrude","SWEPT_EDGE",EDGE,{"disambiguationData":[OSD([subQ1,subQ0]),TDD([makeQuery(id+"F0.imprint","INTERSECT",VERTEX,{"disambiguationData":[OD(1.0)],"derivedFrom":[subQ1,subQ0]})])]});}
            var Q17;
            {var subQ0=sQuery(id+"F0.wireOp",EDGE,"E2.right");var subQ1=sQuery(id+"F0.wireOp",EDGE,"E1.0");Q17=makeQuery(id+"F3.opExtrude","SWEPT_EDGE",EDGE,{"disambiguationData":[OSD([subQ1,subQ0]),TDD([makeQuery(id+"F0.imprint","INTERSECT",VERTEX,{"disambiguationData":[OD(1.0)],"derivedFrom":[subQ1,subQ0]})])]});}
            var Q18;
            {var subQ0=sQuery(id+"F0.wireOp",EDGE,"E3.right");var subQ1=sQuery(id+"F0.wireOp",EDGE,"E1.0");Q18=makeQuery(id+"F3.opExtrude","SWEPT_EDGE",EDGE,{"disambiguationData":[OSD([subQ1,subQ0]),TDD([makeQuery(id+"F0.imprint","INTERSECT",VERTEX,{"disambiguationData":[OD(0.0)],"derivedFrom":[subQ1,subQ0]})])]});}
            var Q19;
            {var subQ0=sQuery(id+"F0.wireOp",EDGE,"E2.right");var subQ1=sQuery(id+"F0.wireOp",EDGE,"E1.0");Q19=makeQuery(id+"F3.opExtrude","SWEPT_EDGE",EDGE,{"disambiguationData":[OSD([subQ1,subQ0]),TDD([makeQuery(id+"F0.imprint","INTERSECT",VERTEX,{"disambiguationData":[OD(0.0)],"derivedFrom":[subQ1,subQ0]})])]});}
            var Q20;
            {var subQ0=sQuery(id+"F0.wireOp",EDGE,"E8.left");var subQ1=sQuery(id+"F0.wireOp",EDGE,"E1.0");Q20=makeQuery(id+"F3.opExtrude","SWEPT_EDGE",EDGE,{"disambiguationData":[OSD([subQ1,subQ0]),TDD([makeQuery(id+"F0.imprint","INTERSECT",VERTEX,{"disambiguationData":[OD(1.0)],"derivedFrom":[subQ1,subQ0]})])]});}
            var Q21;
            {var subQ0=sQuery(id+"F0.wireOp",EDGE,"E9.left");var subQ1=sQuery(id+"F0.wireOp",EDGE,"E1.0");Q21=makeQuery(id+"F3.opExtrude","SWEPT_EDGE",EDGE,{"disambiguationData":[OSD([subQ1,subQ0]),TDD([makeQuery(id+"F0.imprint","INTERSECT",VERTEX,{"disambiguationData":[OD(1.0)],"derivedFrom":[subQ1,subQ0]})])]});}
            var Q22;
            {var subQ0=sQuery(id+"F0.wireOp",EDGE,"E7.top");var subQ1=sQuery(id+"F0.wireOp",EDGE,"E1.0");Q22=makeQuery(id+"F3.opExtrude","SWEPT_EDGE",EDGE,{"disambiguationData":[OSD([subQ1,subQ0]),TDD([makeQuery(id+"F0.imprint","INTERSECT",VERTEX,{"disambiguationData":[OD(1.0)],"derivedFrom":[subQ1,subQ0]})])]});}
            var Q23;
            {var subQ0=sQuery(id+"F0.wireOp",EDGE,"E6.bottom");var subQ1=sQuery(id+"F0.wireOp",EDGE,"E1.0");Q23=makeQuery(id+"F3.opExtrude","SWEPT_EDGE",EDGE,{"disambiguationData":[OSD([subQ1,subQ0]),TDD([makeQuery(id+"F0.imprint","INTERSECT",VERTEX,{"disambiguationData":[OD(0.0)],"derivedFrom":[subQ1,subQ0]})])]});}
            var Q24;
            {var subQ0=sQuery(id+"F0.wireOp",EDGE,"E7.top");var subQ1=sQuery(id+"F0.wireOp",EDGE,"E1.0");var subQ24=sQuery(id+"F1.wireOp",EDGE,"E12");Q24=makeQuery(id+"F7.boolean.opBoolean","INTERSECT",EDGE,{"derivedFrom":[makeQuery(id+"F5.boolean.opBoolean","MERGE",FACE,{"derivedFrom":[makeQuery(id+"F3.boolean.opBoolean","SPLIT",FACE,{"disambiguationData":[TD([makeQuery(id+"F3.opExtrude","SWEPT_FACE",FACE,{"disambiguationData":[OSD([subQ0])]})])],"derivedFrom":makeQuery(id+"F2.opExtrude","SWEPT_FACE",FACE,{"disambiguationData":[OSD([subQ24])]})}),makeQuery(id+"F5.opExtrude","SWEPT_FACE",FACE,{"disambiguationData":[OSD([subQ1]),TDD([makeQuery(id+"F0.imprint","IMPRINT",EDGE,{"disambiguationData":[TD([[makeQuery(id+"F0.imprint","INTERSECT",VERTEX,{"disambiguationData":[OD(0.0)],"derivedFrom":[subQ1,subQ0]}),-1.0]])],"derivedFrom":subQ1})])]})]}),makeQuery(id+"F7.opExtrude","SWEPT_FACE",FACE,{"disambiguationData":[OSD([sQuery(id+"F6.wireOp",EDGE,"E30")])]})]});}
            var Q25;
            {var subQ0=sQuery(id+"F0.wireOp",EDGE,"E7.top");Q25=makeQuery(id+"F7.boolean.opBoolean","INTERSECT",EDGE,{"derivedFrom":[makeQuery(id+"F5.boolean.opBoolean","MERGE",FACE,{"derivedFrom":[makeQuery(id+"F3.opExtrude","SWEPT_FACE",FACE,{"disambiguationData":[OSD([subQ0])]}),makeQuery(id+"F5.opExtrude","SWEPT_FACE",FACE,{"disambiguationData":[OSD([subQ0])]})]}),makeQuery(id+"F7.opExtrude","SWEPT_FACE",FACE,{"disambiguationData":[OSD([sQuery(id+"F6.wireOp",EDGE,"E30")])]})]});}
            var Q26;
            Q26=makeQuery(id+"F5.boolean.opBoolean","COPY",EDGE,{"derivedFrom":makeQuery(id+"F5.opExtrude","SWEPT_EDGE",EDGE,{"disambiguationData":[OSD([sQuery(id+"F0.wireOp",EDGE,"E1.0"),sQuery(id+"F0.wireOp",EDGE,"E9.left")])]})});
            var Q27;
            {var subQ0=sQuery(id+"F0.wireOp",EDGE,"E7.bottom");Q27=makeQuery(id+"F7.boolean.opBoolean","INTERSECT",EDGE,{"derivedFrom":[makeQuery(id+"F5.boolean.opBoolean","MERGE",FACE,{"derivedFrom":[makeQuery(id+"F3.opExtrude","SWEPT_FACE",FACE,{"disambiguationData":[OSD([subQ0])]}),makeQuery(id+"F5.opExtrude","SWEPT_FACE",FACE,{"disambiguationData":[OSD([subQ0])]})]}),makeQuery(id+"F7.opExtrude","SWEPT_FACE",FACE,{"disambiguationData":[OSD([sQuery(id+"F6.wireOp",EDGE,"E30")])]})]});}
            var Q28;
            {var subQ0=sQuery(id+"F0.wireOp",EDGE,"E1.0");var subQ1=sQuery(id+"F0.wireOp",EDGE,"E7.bottom");var subQ24=sQuery(id+"F1.wireOp",EDGE,"E12");Q28=makeQuery(id+"F7.boolean.opBoolean","INTERSECT",EDGE,{"derivedFrom":[makeQuery(id+"F5.boolean.opBoolean","MERGE",FACE,{"derivedFrom":[makeQuery(id+"F3.boolean.opBoolean","SPLIT",FACE,{"disambiguationData":[TD([makeQuery(id+"F3.opExtrude","SWEPT_FACE",FACE,{"disambiguationData":[OSD([subQ1])]})])],"derivedFrom":makeQuery(id+"F2.opExtrude","SWEPT_FACE",FACE,{"disambiguationData":[OSD([subQ24])]})}),makeQuery(id+"F5.opExtrude","SWEPT_FACE",FACE,{"disambiguationData":[OSD([subQ0]),TDD([makeQuery(id+"F0.imprint","IMPRINT",EDGE,{"disambiguationData":[TD([[makeQuery(id+"F0.imprint","INTERSECT",VERTEX,{"disambiguationData":[OD(0.0)],"derivedFrom":[subQ0,sQuery(id+"F0.wireOp",EDGE,"E9.left")]}),-1.0]])],"derivedFrom":subQ0})])]})]}),makeQuery(id+"F7.opExtrude","SWEPT_FACE",FACE,{"disambiguationData":[OSD([sQuery(id+"F6.wireOp",EDGE,"E30")])]})]});}
            var Q29;
            {var subQ0=sQuery(id+"F0.wireOp",EDGE,"E1.0");var subQ1=sQuery(id+"F0.wireOp",EDGE,"E7.bottom");var subQ24=sQuery(id+"F1.wireOp",EDGE,"E12");Q29=makeQuery(id+"F7.boolean.opBoolean","INTERSECT",EDGE,{"disambiguationData":[OD(0.0)],"derivedFrom":[makeQuery(id+"F5.boolean.opBoolean","MERGE",FACE,{"derivedFrom":[makeQuery(id+"F3.boolean.opBoolean","SPLIT",FACE,{"disambiguationData":[TD([makeQuery(id+"F3.opExtrude","SWEPT_FACE",FACE,{"disambiguationData":[OSD([subQ1])]})])],"derivedFrom":makeQuery(id+"F2.opExtrude","SWEPT_FACE",FACE,{"disambiguationData":[OSD([subQ24])]})}),makeQuery(id+"F5.opExtrude","SWEPT_FACE",FACE,{"disambiguationData":[OSD([subQ0]),TDD([makeQuery(id+"F0.imprint","IMPRINT",EDGE,{"disambiguationData":[TD([[makeQuery(id+"F0.imprint","INTERSECT",VERTEX,{"disambiguationData":[OD(0.0)],"derivedFrom":[subQ0,sQuery(id+"F0.wireOp",EDGE,"E9.left")]}),-1.0]])],"derivedFrom":subQ0})])]})]}),makeQuery(id+"F7.opExtrude","SWEPT_FACE",FACE,{"disambiguationData":[OSD([sQuery(id+"F6.wireOp",EDGE,"E25")])]})]});}
            var Q30;
            {var subQ0=sQuery(id+"F0.wireOp",EDGE,"E1.0");var subQ1=sQuery(id+"F0.wireOp",EDGE,"E7.bottom");var subQ24=sQuery(id+"F1.wireOp",EDGE,"E12");Q30=makeQuery(id+"F7.boolean.opBoolean","INTERSECT",EDGE,{"disambiguationData":[OD(1.0)],"derivedFrom":[makeQuery(id+"F5.boolean.opBoolean","MERGE",FACE,{"derivedFrom":[makeQuery(id+"F3.boolean.opBoolean","SPLIT",FACE,{"disambiguationData":[TD([makeQuery(id+"F3.opExtrude","SWEPT_FACE",FACE,{"disambiguationData":[OSD([subQ1])]})])],"derivedFrom":makeQuery(id+"F2.opExtrude","SWEPT_FACE",FACE,{"disambiguationData":[OSD([subQ24])]})}),makeQuery(id+"F5.opExtrude","SWEPT_FACE",FACE,{"disambiguationData":[OSD([subQ0]),TDD([makeQuery(id+"F0.imprint","IMPRINT",EDGE,{"disambiguationData":[TD([[makeQuery(id+"F0.imprint","INTERSECT",VERTEX,{"disambiguationData":[OD(0.0)],"derivedFrom":[subQ0,sQuery(id+"F0.wireOp",EDGE,"E9.left")]}),-1.0]])],"derivedFrom":subQ0})])]})]}),makeQuery(id+"F7.opExtrude","SWEPT_FACE",FACE,{"disambiguationData":[OSD([sQuery(id+"F6.wireOp",EDGE,"E25")])]})]});}
            var Q31;
            {var subQ0=sQuery(id+"F0.wireOp",EDGE,"E1.0");var subQ6=sQuery(id+"F0.wireOp",EDGE,"E2.right");var subQ25=sQuery(id+"F1.wireOp",EDGE,"E12");var subQ30=makeQuery(id+"F0.imprint","INTERSECT",VERTEX,{"disambiguationData":[OD(0.0)],"derivedFrom":[subQ0,subQ6]});var subQ31=makeQuery(id+"F0.imprint","IMPRINT",EDGE,{"disambiguationData":[TD([[subQ30,-1.0]])],"derivedFrom":subQ6});Q31=makeQuery(id+"F7.boolean.opBoolean","INTERSECT",EDGE,{"disambiguationData":[OD(1.0)],"derivedFrom":[makeQuery(id+"F5.boolean.opBoolean","MERGE",FACE,{"derivedFrom":[makeQuery(id+"F3.boolean.opBoolean","SPLIT",FACE,{"disambiguationData":[TD([makeQuery(id+"F3.opExtrude","SWEPT_FACE",FACE,{"disambiguationData":[OSD([subQ6]),TDD([subQ31])]})])],"derivedFrom":makeQuery(id+"F2.opExtrude","SWEPT_FACE",FACE,{"disambiguationData":[OSD([subQ25])]})}),makeQuery(id+"F5.opExtrude","SWEPT_FACE",FACE,{"disambiguationData":[OSD([subQ0]),TDD([makeQuery(id+"F0.imprint","IMPRINT",EDGE,{"disambiguationData":[TD([[makeQuery(id+"F0.imprint","INTERSECT",VERTEX,{"disambiguationData":[OD(0.0)],"derivedFrom":[subQ0,sQuery(id+"F0.wireOp",EDGE,"E3.right")]}),1.0]])],"derivedFrom":subQ0})])]})]}),makeQuery(id+"F7.opExtrude","SWEPT_FACE",FACE,{"disambiguationData":[OSD([sQuery(id+"F6.wireOp",EDGE,"E26")])]})]});}
            var Q32;
            Q32=makeQuery(id+"F7.boolean.opBoolean","INTERSECT",EDGE,{"derivedFrom":[makeQuery(id+"F5.boolean.opBoolean","COPY",FACE,{"derivedFrom":makeQuery(id+"F5.opExtrude","SWEPT_FACE",FACE,{"disambiguationData":[OSD([sQuery(id+"F0.wireOp",EDGE,"E3.right")])]})}),makeQuery(id+"F7.opExtrude","SWEPT_FACE",FACE,{"disambiguationData":[OSD([sQuery(id+"F6.wireOp",EDGE,"E26")])]})]});
            var Q33;
            {var subQ0=sQuery(id+"F0.wireOp",EDGE,"E1.0");var subQ6=sQuery(id+"F0.wireOp",EDGE,"E2.right");var subQ25=sQuery(id+"F1.wireOp",EDGE,"E12");var subQ30=makeQuery(id+"F0.imprint","INTERSECT",VERTEX,{"disambiguationData":[OD(0.0)],"derivedFrom":[subQ0,subQ6]});var subQ31=makeQuery(id+"F0.imprint","IMPRINT",EDGE,{"disambiguationData":[TD([[subQ30,-1.0]])],"derivedFrom":subQ6});Q33=makeQuery(id+"F7.boolean.opBoolean","INTERSECT",EDGE,{"disambiguationData":[OD(0.0)],"derivedFrom":[makeQuery(id+"F5.boolean.opBoolean","MERGE",FACE,{"derivedFrom":[makeQuery(id+"F3.boolean.opBoolean","SPLIT",FACE,{"disambiguationData":[TD([makeQuery(id+"F3.opExtrude","SWEPT_FACE",FACE,{"disambiguationData":[OSD([subQ6]),TDD([subQ31])]})])],"derivedFrom":makeQuery(id+"F2.opExtrude","SWEPT_FACE",FACE,{"disambiguationData":[OSD([subQ25])]})}),makeQuery(id+"F5.opExtrude","SWEPT_FACE",FACE,{"disambiguationData":[OSD([subQ0]),TDD([makeQuery(id+"F0.imprint","IMPRINT",EDGE,{"disambiguationData":[TD([[makeQuery(id+"F0.imprint","INTERSECT",VERTEX,{"disambiguationData":[OD(0.0)],"derivedFrom":[subQ0,sQuery(id+"F0.wireOp",EDGE,"E3.right")]}),1.0]])],"derivedFrom":subQ0})])]})]}),makeQuery(id+"F7.opExtrude","SWEPT_FACE",FACE,{"disambiguationData":[OSD([sQuery(id+"F6.wireOp",EDGE,"E26")])]})]});}
            var Q34;
            {var subQ3=sQuery(id+"F0.wireOp",EDGE,"E2.right");var subQ6=sQuery(id+"F0.wireOp",EDGE,"E1.0");var subQ7=makeQuery(id+"F0.imprint","INTERSECT",VERTEX,{"disambiguationData":[OD(1.0)],"derivedFrom":[subQ6,subQ3]});var subQ8=makeQuery(id+"F0.imprint","IMPRINT",EDGE,{"disambiguationData":[TD([[subQ7,1.0]])],"derivedFrom":subQ3});var subQ24=sQuery(id+"F1.wireOp",EDGE,"E12");Q34=makeQuery(id+"F7.boolean.opBoolean","INTERSECT",EDGE,{"disambiguationData":[OD(1.0)],"derivedFrom":[makeQuery(id+"F3.boolean.opBoolean","SPLIT",FACE,{"disambiguationData":[TD([makeQuery(id+"F3.opExtrude","SWEPT_FACE",FACE,{"disambiguationData":[OSD([subQ3]),TDD([subQ8])]})])],"derivedFrom":makeQuery(id+"F2.opExtrude","SWEPT_FACE",FACE,{"disambiguationData":[OSD([subQ24])]})}),makeQuery(id+"F7.opExtrude","SWEPT_FACE",FACE,{"disambiguationData":[OSD([sQuery(id+"F6.wireOp",EDGE,"E27")])]})]});}
            var Q35;
            {var subQ3=sQuery(id+"F0.wireOp",EDGE,"E2.right");var subQ6=sQuery(id+"F0.wireOp",EDGE,"E1.0");var subQ7=makeQuery(id+"F0.imprint","INTERSECT",VERTEX,{"disambiguationData":[OD(1.0)],"derivedFrom":[subQ6,subQ3]});var subQ8=makeQuery(id+"F0.imprint","IMPRINT",EDGE,{"disambiguationData":[TD([[subQ7,1.0]])],"derivedFrom":subQ3});var subQ24=sQuery(id+"F1.wireOp",EDGE,"E12");Q35=makeQuery(id+"F7.boolean.opBoolean","INTERSECT",EDGE,{"disambiguationData":[OD(0.0)],"derivedFrom":[makeQuery(id+"F3.boolean.opBoolean","SPLIT",FACE,{"disambiguationData":[TD([makeQuery(id+"F3.opExtrude","SWEPT_FACE",FACE,{"disambiguationData":[OSD([subQ3]),TDD([subQ8])]})])],"derivedFrom":makeQuery(id+"F2.opExtrude","SWEPT_FACE",FACE,{"disambiguationData":[OSD([subQ24])]})}),makeQuery(id+"F7.opExtrude","SWEPT_FACE",FACE,{"disambiguationData":[OSD([sQuery(id+"F6.wireOp",EDGE,"E27")])]})]});}
            var Q36;
            {var subQ3=sQuery(id+"F0.wireOp",EDGE,"E2.right");var subQ6=sQuery(id+"F0.wireOp",EDGE,"E1.0");var subQ7=makeQuery(id+"F0.imprint","INTERSECT",VERTEX,{"disambiguationData":[OD(1.0)],"derivedFrom":[subQ6,subQ3]});var subQ8=makeQuery(id+"F0.imprint","IMPRINT",EDGE,{"disambiguationData":[TD([[subQ7,1.0]])],"derivedFrom":subQ3});var subQ24=sQuery(id+"F1.wireOp",EDGE,"E12");Q36=makeQuery(id+"F7.boolean.opBoolean","INTERSECT",EDGE,{"disambiguationData":[OD(0.0)],"derivedFrom":[makeQuery(id+"F3.boolean.opBoolean","SPLIT",FACE,{"disambiguationData":[TD([makeQuery(id+"F3.opExtrude","SWEPT_FACE",FACE,{"disambiguationData":[OSD([subQ3]),TDD([subQ8])]})])],"derivedFrom":makeQuery(id+"F2.opExtrude","SWEPT_FACE",FACE,{"disambiguationData":[OSD([subQ24])]})}),makeQuery(id+"F7.opExtrude","SWEPT_FACE",FACE,{"disambiguationData":[OSD([sQuery(id+"F6.wireOp",EDGE,"E28")])]})]});}
            var Q37;
            {var subQ3=sQuery(id+"F0.wireOp",EDGE,"E2.right");var subQ6=sQuery(id+"F0.wireOp",EDGE,"E1.0");var subQ7=makeQuery(id+"F0.imprint","INTERSECT",VERTEX,{"disambiguationData":[OD(1.0)],"derivedFrom":[subQ6,subQ3]});var subQ8=makeQuery(id+"F0.imprint","IMPRINT",EDGE,{"disambiguationData":[TD([[subQ7,1.0]])],"derivedFrom":subQ3});var subQ24=sQuery(id+"F1.wireOp",EDGE,"E12");Q37=makeQuery(id+"F7.boolean.opBoolean","INTERSECT",EDGE,{"disambiguationData":[OD(1.0)],"derivedFrom":[makeQuery(id+"F3.boolean.opBoolean","SPLIT",FACE,{"disambiguationData":[TD([makeQuery(id+"F3.opExtrude","SWEPT_FACE",FACE,{"disambiguationData":[OSD([subQ3]),TDD([subQ8])]})])],"derivedFrom":makeQuery(id+"F2.opExtrude","SWEPT_FACE",FACE,{"disambiguationData":[OSD([subQ24])]})}),makeQuery(id+"F7.opExtrude","SWEPT_FACE",FACE,{"disambiguationData":[OSD([sQuery(id+"F6.wireOp",EDGE,"E28")])]})]});}
            var Q38;
            {var subQ1=sQuery(id+"F0.wireOp",EDGE,"E2.left");var subQ6=sQuery(id+"F0.wireOp",EDGE,"E1.0");var subQ9=makeQuery(id+"F0.imprint","INTERSECT",VERTEX,{"disambiguationData":[OD(1.0)],"derivedFrom":[subQ6,subQ1]});var subQ10=makeQuery(id+"F0.imprint","IMPRINT",EDGE,{"disambiguationData":[TD([[subQ9,1.0]])],"derivedFrom":subQ1});var subQ24=sQuery(id+"F1.wireOp",EDGE,"E12");Q38=makeQuery(id+"F7.boolean.opBoolean","INTERSECT",EDGE,{"disambiguationData":[OD(0.0)],"derivedFrom":[makeQuery(id+"F3.boolean.opBoolean","SPLIT",FACE,{"disambiguationData":[TD([makeQuery(id+"F3.opExtrude","SWEPT_FACE",FACE,{"disambiguationData":[OSD([subQ1]),TDD([subQ10])]})])],"derivedFrom":makeQuery(id+"F2.opExtrude","SWEPT_FACE",FACE,{"disambiguationData":[OSD([subQ24])]})}),makeQuery(id+"F7.opExtrude","SWEPT_FACE",FACE,{"disambiguationData":[OSD([sQuery(id+"F6.wireOp",EDGE,"E29")])]})]});}
            var Q39;
            {var subQ1=sQuery(id+"F0.wireOp",EDGE,"E2.left");var subQ6=sQuery(id+"F0.wireOp",EDGE,"E1.0");var subQ9=makeQuery(id+"F0.imprint","INTERSECT",VERTEX,{"disambiguationData":[OD(1.0)],"derivedFrom":[subQ6,subQ1]});var subQ10=makeQuery(id+"F0.imprint","IMPRINT",EDGE,{"disambiguationData":[TD([[subQ9,1.0]])],"derivedFrom":subQ1});var subQ24=sQuery(id+"F1.wireOp",EDGE,"E12");Q39=makeQuery(id+"F7.boolean.opBoolean","INTERSECT",EDGE,{"disambiguationData":[OD(1.0)],"derivedFrom":[makeQuery(id+"F3.boolean.opBoolean","SPLIT",FACE,{"disambiguationData":[TD([makeQuery(id+"F3.opExtrude","SWEPT_FACE",FACE,{"disambiguationData":[OSD([subQ1]),TDD([subQ10])]})])],"derivedFrom":makeQuery(id+"F2.opExtrude","SWEPT_FACE",FACE,{"disambiguationData":[OSD([subQ24])]})}),makeQuery(id+"F7.opExtrude","SWEPT_FACE",FACE,{"disambiguationData":[OSD([sQuery(id+"F6.wireOp",EDGE,"E29")])]})]});}
            fillet(context, id + "F8", {"entities" : qUnion([Q0, Q1, Q2, Q3, Q4, Q5, Q6, Q7, Q8, Q9, Q10, Q11, Q12, Q13, Q14, Q15, Q16, Q17, Q18, Q19, Q20, Q21, Q22, Q23, Q24, Q25, Q26, Q27, Q28, Q29, Q30, Q31, Q32, Q33, Q34, Q35, Q36, Q37, Q38, Q39]), "radius" : 1 * mm, "tangentPropagation" : true, "allowEdgeOverflow" : false});
        }
        {
            var Q0;
            {var subQ0=sQuery(id+"F6.wireOp",EDGE,"E31");var subQ1=sQuery(id+"F6.wireOp",EDGE,"E13");var subQ2=makeQuery(id+"F6.imprint","INTERSECT",VERTEX,{"disambiguationData":[OD(0.0)],"derivedFrom":[subQ1,subQ0]});Q0=makeQuery(id+"F6.imprint","IMPRINT",FACE,{"disambiguationData":[TD([[makeQuery(id+"F6.imprint","IMPRINT",EDGE,{"disambiguationData":[TD([[subQ2,-1.0]])],"derivedFrom":subQ1}),-1.0]])]});}
            var Q1;
            {var subQ0=sQuery(id+"F6.wireOp",EDGE,"E31");var subQ1=sQuery(id+"F6.wireOp",EDGE,"E13");var subQ2=makeQuery(id+"F6.imprint","INTERSECT",VERTEX,{"disambiguationData":[OD(0.0)],"derivedFrom":[subQ1,subQ0]});Q1=makeQuery(id+"F6.imprint","IMPRINT",FACE,{"disambiguationData":[TD([[makeQuery(id+"F6.imprint","IMPRINT",EDGE,{"disambiguationData":[TD([[subQ2,-1.0]])],"derivedFrom":subQ1}),1.0]])]});}
            var Q2;
            {var subQ0=sQuery(id+"F6.wireOp",EDGE,"E32");var subQ1=sQuery(id+"F6.wireOp",EDGE,"E13");var subQ2=makeQuery(id+"F6.imprint","INTERSECT",VERTEX,{"disambiguationData":[OD(0.0)],"derivedFrom":[subQ1,subQ0]});Q2=makeQuery(id+"F6.imprint","IMPRINT",FACE,{"disambiguationData":[TD([[makeQuery(id+"F6.imprint","IMPRINT",EDGE,{"disambiguationData":[TD([[subQ2,-1.0]])],"derivedFrom":subQ1}),-1.0]])]});}
            var Q3;
            {var subQ0=sQuery(id+"F6.wireOp",EDGE,"E32");var subQ1=sQuery(id+"F6.wireOp",EDGE,"E13");var subQ2=makeQuery(id+"F6.imprint","INTERSECT",VERTEX,{"disambiguationData":[OD(0.0)],"derivedFrom":[subQ1,subQ0]});Q3=makeQuery(id+"F6.imprint","IMPRINT",FACE,{"disambiguationData":[TD([[makeQuery(id+"F6.imprint","IMPRINT",EDGE,{"disambiguationData":[TD([[subQ2,-1.0]])],"derivedFrom":subQ1}),1.0]])]});}
            var Q4;
            {var subQ0=sQuery(id+"F6.wireOp",EDGE,"E33");var subQ1=sQuery(id+"F6.wireOp",EDGE,"E13");var subQ2=makeQuery(id+"F6.imprint","INTERSECT",VERTEX,{"disambiguationData":[OD(0.0)],"derivedFrom":[subQ1,subQ0]});Q4=makeQuery(id+"F6.imprint","IMPRINT",FACE,{"disambiguationData":[TD([[makeQuery(id+"F6.imprint","IMPRINT",EDGE,{"disambiguationData":[TD([[subQ2,-1.0]])],"derivedFrom":subQ1}),1.0]])]});}
            var Q5;
            {var subQ0=sQuery(id+"F6.wireOp",EDGE,"E33");var subQ1=sQuery(id+"F6.wireOp",EDGE,"E13");var subQ2=makeQuery(id+"F6.imprint","INTERSECT",VERTEX,{"disambiguationData":[OD(0.0)],"derivedFrom":[subQ1,subQ0]});Q5=makeQuery(id+"F6.imprint","IMPRINT",FACE,{"disambiguationData":[TD([[makeQuery(id+"F6.imprint","IMPRINT",EDGE,{"disambiguationData":[TD([[subQ2,-1.0]])],"derivedFrom":subQ1}),-1.0]])]});}
            var Q6;
            {var subQ0=sQuery(id+"F6.wireOp",EDGE,"E34");var subQ1=sQuery(id+"F6.wireOp",EDGE,"E13");var subQ2=makeQuery(id+"F6.imprint","INTERSECT",VERTEX,{"disambiguationData":[OD(0.0)],"derivedFrom":[subQ1,subQ0]});Q6=makeQuery(id+"F6.imprint","IMPRINT",FACE,{"disambiguationData":[TD([[makeQuery(id+"F6.imprint","IMPRINT",EDGE,{"disambiguationData":[TD([[subQ2,-1.0]])],"derivedFrom":subQ1}),1.0]])]});}
            var Q7;
            {var subQ0=sQuery(id+"F6.wireOp",EDGE,"E34");var subQ1=sQuery(id+"F6.wireOp",EDGE,"E13");var subQ2=makeQuery(id+"F6.imprint","INTERSECT",VERTEX,{"disambiguationData":[OD(0.0)],"derivedFrom":[subQ1,subQ0]});Q7=makeQuery(id+"F6.imprint","IMPRINT",FACE,{"disambiguationData":[TD([[makeQuery(id+"F6.imprint","IMPRINT",EDGE,{"disambiguationData":[TD([[subQ2,-1.0]])],"derivedFrom":subQ1}),-1.0]])]});}
            var Q8;
            {var subQ1=sQuery(id+"F6.wireOp",EDGE,"E36.bottom");Q8=makeQuery(id+"F6.imprint","IMPRINT",FACE,{"disambiguationData":[TD([[makeQuery(id+"F6.imprint","IMPRINT",EDGE,{"derivedFrom":subQ1}),-1.0]])]});}
            var Q9;
            {var subQ0=sQuery(id+"F6.wireOp",EDGE,"E36.top");var subQ1=sQuery(id+"F6.wireOp",EDGE,"E13");var subQ2=makeQuery(id+"F6.imprint","INTERSECT",VERTEX,{"derivedFrom":[subQ1,subQ0]});Q9=makeQuery(id+"F6.imprint","IMPRINT",FACE,{"disambiguationData":[TD([[makeQuery(id+"F6.imprint","IMPRINT",EDGE,{"disambiguationData":[TD([[subQ2,-1.0]])],"derivedFrom":subQ1}),1.0]])]});}
            var Q10;
            {var subQ0=sQuery(id+"F6.wireOp",EDGE,"E35");var subQ1=sQuery(id+"F6.wireOp",EDGE,"E13");var subQ2=makeQuery(id+"F6.imprint","INTERSECT",VERTEX,{"disambiguationData":[OD(0.0)],"derivedFrom":[subQ1,subQ0]});Q10=makeQuery(id+"F6.imprint","IMPRINT",FACE,{"disambiguationData":[TD([[makeQuery(id+"F6.imprint","IMPRINT",EDGE,{"disambiguationData":[TD([[subQ2,-1.0]])],"derivedFrom":subQ1}),-1.0]])]});}
            var Q11;
            {var subQ0=sQuery(id+"F6.wireOp",EDGE,"E35");var subQ1=sQuery(id+"F6.wireOp",EDGE,"E13");var subQ2=makeQuery(id+"F6.imprint","INTERSECT",VERTEX,{"disambiguationData":[OD(0.0)],"derivedFrom":[subQ1,subQ0]});Q11=makeQuery(id+"F6.imprint","IMPRINT",FACE,{"disambiguationData":[TD([[makeQuery(id+"F6.imprint","IMPRINT",EDGE,{"disambiguationData":[TD([[subQ2,-1.0]])],"derivedFrom":subQ1}),1.0]])]});}
            extrude(context, id + "F9", {"entities" : qUnion([Q0, Q1, Q2, Q3, Q4, Q5, Q6, Q7, Q8, Q9, Q10, Q11]), "operationType" : NewBodyOperationType.ADD, "depth" : 11 * mm, "offsetDistance" : 25 * mm, "hasDraft" : true, "draftAngle" : .9 * degree, "draftPullDirection" : true});
        }
        {
            var Q0;
            Q0=makeQuery(id+"F9.opExtrude","CAP_EDGE",EDGE,{"disambiguationData":[OSD([sQuery(id+"F6.wireOp",EDGE,"E35")])],"isStart":false});
            var Q1;
            Q1=makeQuery(id+"F9.opExtrude","CAP_FACE",FACE,{"disambiguationData":[OSD([sQuery(id+"F6.wireOp",EDGE,"E31")])],"isStart":false});
            var Q2;
            Q2=makeQuery(id+"F9.opExtrude","CAP_FACE",FACE,{"disambiguationData":[OSD([sQuery(id+"F6.wireOp",EDGE,"E32")])],"isStart":false});
            var Q3;
            Q3=makeQuery(id+"F9.opExtrude","CAP_FACE",FACE,{"disambiguationData":[OSD([sQuery(id+"F6.wireOp",EDGE,"E33")])],"isStart":false});
            var Q4;
            Q4=makeQuery(id+"F9.opExtrude","CAP_FACE",FACE,{"disambiguationData":[OSD([sQuery(id+"F6.wireOp",EDGE,"E34")])],"isStart":false});
            var Q5;
            Q5=makeQuery(id+"F9.opExtrude","CAP_EDGE",EDGE,{"disambiguationData":[OSD([sQuery(id+"F6.wireOp",EDGE,"E36.left")])],"isStart":false});
            var Q6;
            Q6=makeQuery(id+"F9.opExtrude","CAP_EDGE",EDGE,{"disambiguationData":[OSD([sQuery(id+"F6.wireOp",EDGE,"E36.right")])],"isStart":false});
            var Q7;
            Q7=makeQuery(id+"F9.opExtrude","CAP_EDGE",EDGE,{"disambiguationData":[OSD([sQuery(id+"F6.wireOp",EDGE,"E36.bottom")])],"isStart":false});
            var Q8;
            Q8=makeQuery(id+"F9.opExtrude","CAP_EDGE",EDGE,{"disambiguationData":[OSD([sQuery(id+"F6.wireOp",EDGE,"E36.top")])],"isStart":false});
            fillet(context, id + "F10", {"entities" : qUnion([Q0, Q1, Q2, Q3, Q4, Q5, Q6, Q7, Q8]), "radius" : .45 * mm, "tangentPropagation" : true, "allowEdgeOverflow" : false});
        }
        {
            var Q0;
            {var subQ0=sQuery(id+"F6.wireOp",EDGE,"E35");var subQ1=sQuery(id+"F6.wireOp",EDGE,"E13");var subQ2=makeQuery(id+"F6.imprint","INTERSECT",VERTEX,{"disambiguationData":[OD(0.0)],"derivedFrom":[subQ1,subQ0]});Q0=makeQuery(id+"F6.imprint","IMPRINT",FACE,{"disambiguationData":[TD([[makeQuery(id+"F6.imprint","IMPRINT",EDGE,{"disambiguationData":[TD([[subQ2,-1.0]])],"derivedFrom":subQ1}),-1.0]])]});}
            var Q1;
            {var subQ0=sQuery(id+"F6.wireOp",EDGE,"E35");var subQ1=sQuery(id+"F6.wireOp",EDGE,"E13");var subQ2=makeQuery(id+"F6.imprint","INTERSECT",VERTEX,{"disambiguationData":[OD(0.0)],"derivedFrom":[subQ1,subQ0]});Q1=makeQuery(id+"F6.imprint","IMPRINT",FACE,{"disambiguationData":[TD([[makeQuery(id+"F6.imprint","IMPRINT",EDGE,{"disambiguationData":[TD([[subQ2,-1.0]])],"derivedFrom":subQ1}),1.0]])]});}
            var Q2;
            {var subQ1=sQuery(id+"F6.wireOp",EDGE,"E36.bottom");Q2=makeQuery(id+"F6.imprint","IMPRINT",FACE,{"disambiguationData":[TD([[makeQuery(id+"F6.imprint","IMPRINT",EDGE,{"derivedFrom":subQ1}),-1.0]])]});}
            var Q3;
            {var subQ0=sQuery(id+"F6.wireOp",EDGE,"E36.top");var subQ1=sQuery(id+"F6.wireOp",EDGE,"E13");var subQ2=makeQuery(id+"F6.imprint","INTERSECT",VERTEX,{"derivedFrom":[subQ1,subQ0]});Q3=makeQuery(id+"F6.imprint","IMPRINT",FACE,{"disambiguationData":[TD([[makeQuery(id+"F6.imprint","IMPRINT",EDGE,{"disambiguationData":[TD([[subQ2,-1.0]])],"derivedFrom":subQ1}),1.0]])]});}
            var Q4;
            {var subQ0=sQuery(id+"F6.wireOp",EDGE,"E34");var subQ1=sQuery(id+"F6.wireOp",EDGE,"E13");var subQ2=makeQuery(id+"F6.imprint","INTERSECT",VERTEX,{"disambiguationData":[OD(0.0)],"derivedFrom":[subQ1,subQ0]});Q4=makeQuery(id+"F6.imprint","IMPRINT",FACE,{"disambiguationData":[TD([[makeQuery(id+"F6.imprint","IMPRINT",EDGE,{"disambiguationData":[TD([[subQ2,-1.0]])],"derivedFrom":subQ1}),1.0]])]});}
            var Q5;
            {var subQ0=sQuery(id+"F6.wireOp",EDGE,"E34");var subQ1=sQuery(id+"F6.wireOp",EDGE,"E13");var subQ2=makeQuery(id+"F6.imprint","INTERSECT",VERTEX,{"disambiguationData":[OD(0.0)],"derivedFrom":[subQ1,subQ0]});Q5=makeQuery(id+"F6.imprint","IMPRINT",FACE,{"disambiguationData":[TD([[makeQuery(id+"F6.imprint","IMPRINT",EDGE,{"disambiguationData":[TD([[subQ2,-1.0]])],"derivedFrom":subQ1}),-1.0]])]});}
            var Q6;
            {var subQ0=sQuery(id+"F6.wireOp",EDGE,"E33");var subQ1=sQuery(id+"F6.wireOp",EDGE,"E13");var subQ2=makeQuery(id+"F6.imprint","INTERSECT",VERTEX,{"disambiguationData":[OD(0.0)],"derivedFrom":[subQ1,subQ0]});Q6=makeQuery(id+"F6.imprint","IMPRINT",FACE,{"disambiguationData":[TD([[makeQuery(id+"F6.imprint","IMPRINT",EDGE,{"disambiguationData":[TD([[subQ2,-1.0]])],"derivedFrom":subQ1}),1.0]])]});}
            var Q7;
            {var subQ0=sQuery(id+"F6.wireOp",EDGE,"E33");var subQ1=sQuery(id+"F6.wireOp",EDGE,"E13");var subQ2=makeQuery(id+"F6.imprint","INTERSECT",VERTEX,{"disambiguationData":[OD(0.0)],"derivedFrom":[subQ1,subQ0]});Q7=makeQuery(id+"F6.imprint","IMPRINT",FACE,{"disambiguationData":[TD([[makeQuery(id+"F6.imprint","IMPRINT",EDGE,{"disambiguationData":[TD([[subQ2,-1.0]])],"derivedFrom":subQ1}),-1.0]])]});}
            var Q8;
            {var subQ0=sQuery(id+"F6.wireOp",EDGE,"E32");var subQ1=sQuery(id+"F6.wireOp",EDGE,"E13");var subQ2=makeQuery(id+"F6.imprint","INTERSECT",VERTEX,{"disambiguationData":[OD(0.0)],"derivedFrom":[subQ1,subQ0]});Q8=makeQuery(id+"F6.imprint","IMPRINT",FACE,{"disambiguationData":[TD([[makeQuery(id+"F6.imprint","IMPRINT",EDGE,{"disambiguationData":[TD([[subQ2,-1.0]])],"derivedFrom":subQ1}),1.0]])]});}
            var Q9;
            {var subQ0=sQuery(id+"F6.wireOp",EDGE,"E32");var subQ1=sQuery(id+"F6.wireOp",EDGE,"E13");var subQ2=makeQuery(id+"F6.imprint","INTERSECT",VERTEX,{"disambiguationData":[OD(0.0)],"derivedFrom":[subQ1,subQ0]});Q9=makeQuery(id+"F6.imprint","IMPRINT",FACE,{"disambiguationData":[TD([[makeQuery(id+"F6.imprint","IMPRINT",EDGE,{"disambiguationData":[TD([[subQ2,-1.0]])],"derivedFrom":subQ1}),-1.0]])]});}
            var Q10;
            {var subQ0=sQuery(id+"F6.wireOp",EDGE,"E31");var subQ1=sQuery(id+"F6.wireOp",EDGE,"E13");var subQ2=makeQuery(id+"F6.imprint","INTERSECT",VERTEX,{"disambiguationData":[OD(0.0)],"derivedFrom":[subQ1,subQ0]});Q10=makeQuery(id+"F6.imprint","IMPRINT",FACE,{"disambiguationData":[TD([[makeQuery(id+"F6.imprint","IMPRINT",EDGE,{"disambiguationData":[TD([[subQ2,-1.0]])],"derivedFrom":subQ1}),-1.0]])]});}
            var Q11;
            {var subQ0=sQuery(id+"F6.wireOp",EDGE,"E31");var subQ1=sQuery(id+"F6.wireOp",EDGE,"E13");var subQ2=makeQuery(id+"F6.imprint","INTERSECT",VERTEX,{"disambiguationData":[OD(0.0)],"derivedFrom":[subQ1,subQ0]});Q11=makeQuery(id+"F6.imprint","IMPRINT",FACE,{"disambiguationData":[TD([[makeQuery(id+"F6.imprint","IMPRINT",EDGE,{"disambiguationData":[TD([[subQ2,-1.0]])],"derivedFrom":subQ1}),1.0]])]});}
            extrude(context, id + "F11", {"entities" : qUnion([Q0, Q1, Q2, Q3, Q4, Q5, Q6, Q7, Q8, Q9, Q10, Q11]), "operationType" : NewBodyOperationType.REMOVE, "depth" : 3 * mm, "offsetDistance" : 25 * mm});
        }
        {
            var Q0;
            Q0=qCreatedBy(makeId("Top.planeOp"),FACE);
            var sketch = newSketch(context, id + "F12", { "sketchPlane" : qUnion([Q0])});
            skCircle(sketch, "E37", {"center": v(0, 0) * mm, "radius": 17.33 * mm});
            skSolve(sketch);
        }
        {
            var Q0;
            Q0=makeQuery(id+"F12.imprint","IMPRINT",FACE,{"disambiguationData":[TD([[makeQuery(id+"F12.imprint","IMPRINT",EDGE,{"derivedFrom":sQuery(id+"F12.wireOp",EDGE,"E37")}),1.0]])]});
            extrude(context, id + "F13", {"entities" : qUnion([Q0]), "operationType" : NewBodyOperationType.REMOVE, "depth" : 1 * mm, "offsetDistance" : 25 * mm});
        }
    });
